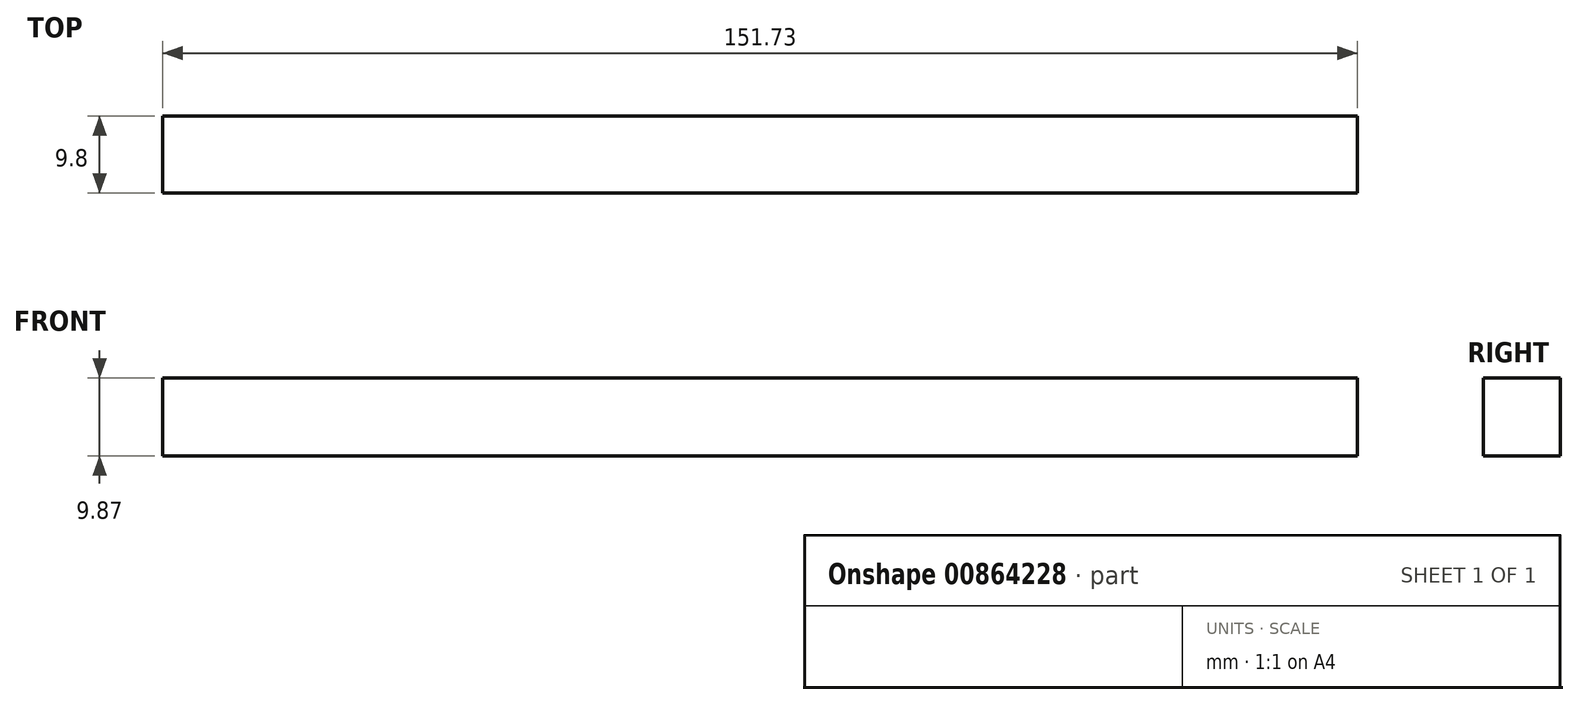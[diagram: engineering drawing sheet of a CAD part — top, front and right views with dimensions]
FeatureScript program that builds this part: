
annotation { "Feature Type Name" : "Feature", "Feature Type Description" : "" }
export const myFeature = defineFeature(function(context is Context, id is Id, definition is map)
    precondition{}
    {
        {
            var Q0;
            Q0=qCreatedBy(makeId("Front.planeOp"),FACE);
            var sketch = newSketch(context, id + "F0", { "sketchPlane" : qUnion([Q0])});
            skLineSegment(sketch, "E0", {"start": v(-99.8, 9.4) * mm, "end": v(51.94, 9.4) * mm});
            skLineSegment(sketch, "E1", {"start": v(51.94, 9.4) * mm, "end": v(51.94, 19.27) * mm});
            skLineSegment(sketch, "E2", {"start": v(51.94, 19.27) * mm, "end": v(-99.8, 19.27) * mm});
            skLineSegment(sketch, "E3", {"start": v(-99.8, 19.27) * mm, "end": v(-99.8, 9.4) * mm});
            skSolve(sketch);
        }
        {
            var Q0;
            Q0=makeQuery(id+"F0.imprint","IMPRINT",FACE,{"disambiguationData":[TD([[makeQuery(id+"F0.imprint","IMPRINT",EDGE,{"derivedFrom":sQuery(id+"F0.wireOp",EDGE,"E0")}),1.0]])]});
            extrude(context, id + "F1", {"entities" : qUnion([Q0]), "depth" : 9.8 * mm, "offsetDistance" : 25.4 * mm});
        }
    });
